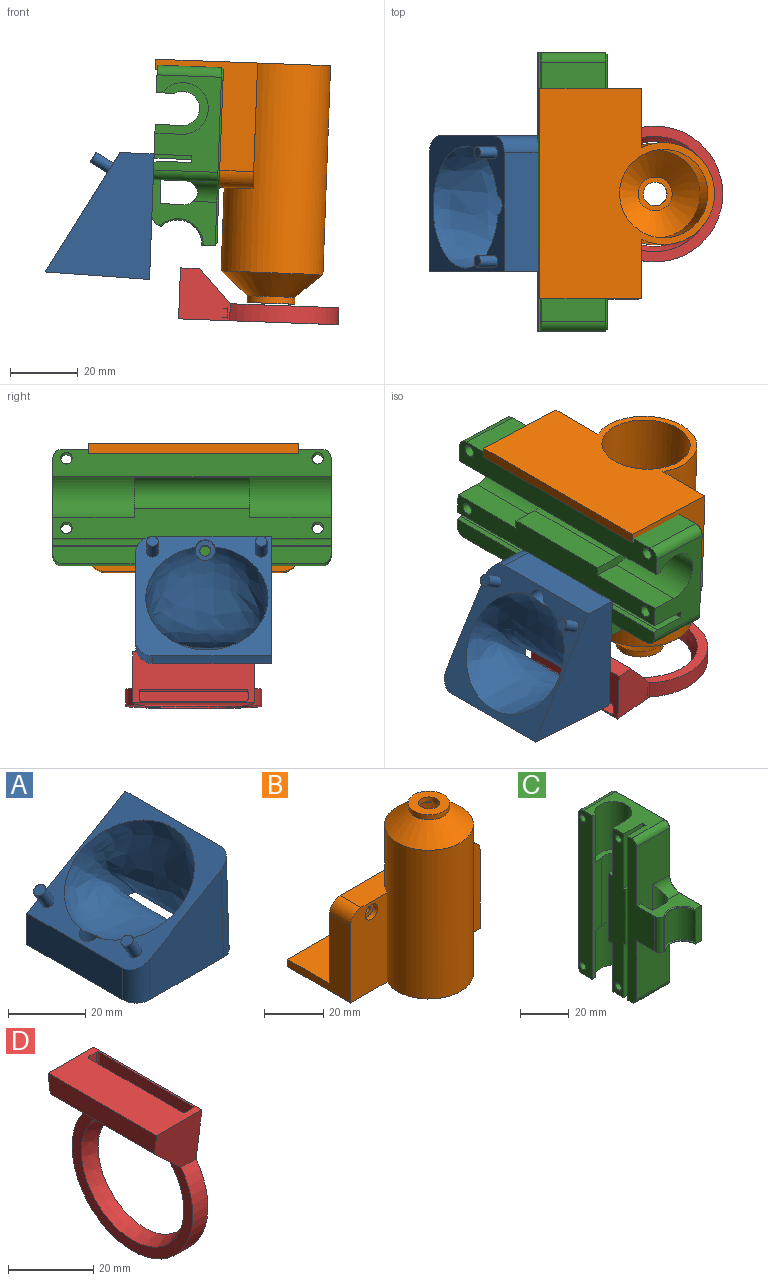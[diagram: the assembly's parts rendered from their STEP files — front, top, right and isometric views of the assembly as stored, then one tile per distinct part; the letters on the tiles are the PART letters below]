
ASSEMBLY  parts=4 mates=5
PART A: 17 faces, bbox 37.6x40.6x31.5 mm
  f0: plane 40.57x36.5mm, normal (-0.5,0,0.87), area 601.5mm2, adj f1,f3,f4,f5,f6,f8,f10,f11
  f1: plane 35x30.74mm, normal (1,0,0.03), area 1076.7mm2, adj f0,f2,f11,f16
  f2: plane 40.34x37.34mm, normal (0,0,-1), area 1343.6mm2, adj f1,f3,f4,f5,f10,f11,f15,f16
  f3: plane 35x10mm, normal (-1,0,0), area 350mm2, adj f0,f2,f10,f16
  f4: plane 27.91x27mm, normal (0,-1,0), area 544.5mm2, adj f0,f2,f10,f11
  f5: bspline ~35.97x33.55mm, area 2475.7mm2, adj f0,f2,f13
  f6: cylinder r=1.7mm len=6.9mm, axis (0.5,0,-0.87), area 64.1mm2, adj f0,f7
  f7: plane 3.4x2.94mm, normal (-0.5,0,0.87), area 9.1mm2, adj f6
  f8: cylinder r=1.7mm len=6.9mm, axis (0.5,0,-0.87), area 64.1mm2, adj f0,f9
  f9: plane 3.4x2.94mm, normal (-0.5,0,0.87), area 9.1mm2, adj f8
  f10: cylinder r=5mm len=12.89mm, axis (0,0,1), area 86.8mm2, adj f0,f2,f3,f4
  f11: cylinder r=5mm len=30.92mm, axis (0.03,0,-1), area 233.3mm2, adj f0,f1,f2,f4
  f12: cylinder r=1.6mm len=5.5mm, axis (0,0,-1), area 55.3mm2, adj f14,f15
  f13: cylinder r=3mm len=6mm, axis (0,0,-1), area 80.9mm2, adj f0,f5,f14
  f14: plane 6x6mm, normal (0,0,1), area 20.2mm2, adj f12,f13
  f15: cone r=1.6mm half-angle=45deg, axis (0,0,-1), area 8.2mm2, adj f2,f12
  f16: plane 37x30.74mm, normal (0,1,0), area 748.4mm2, adj f0,f1,f2,f3
PART B: 25 faces, bbox 62x51.5x70.6 mm
  f0: plane 62x51.5mm, normal (0,0,-1), area 1871.2mm2, adj f3,f4,f7,f13,f14,f15,f16
  f1: plane 62x20mm, normal (0,0,1), area 1240mm2, adj f2,f4,f14,f15
  f2: plane 62x34mm, normal (0,1,0), area 2085mm2, adj f1,f5,f6,f8,f14,f15,f17,f18
  f3: plane 37x17.48mm, normal (0,-1,0), area 613.2mm2, adj f0,f8,f10,f15,f16,f17
  f4: plane 62x3mm, normal (0,1,0), area 186mm2, adj f0,f1,f14,f15
  f5: cylinder r=1.4mm len=8mm, axis (0,-1,0), area 70.4mm2, adj f2,f11
  f6: cylinder r=1.4mm len=8mm, axis (0,-1,0), area 70.4mm2, adj f2,f9
  f7: plane 37x17.48mm, normal (0,-1,0), area 613.2mm2, adj f0,f8,f12,f14,f16,f18
  f8: plane 52x10mm, normal (0,0,1), area 355.3mm2, adj f2,f3,f7,f16,f17,f18
  f9: plane 6x6mm, normal (0,-1,0), area 22.1mm2, adj f6,f10
  f10: cylinder r=3mm len=6mm, axis (0,-1,0), area 37.7mm2, adj f3,f9
  f11: plane 6x6mm, normal (0,-1,0), area 22.1mm2, adj f5,f12
  f12: cylinder r=3mm len=6mm, axis (0,-1,0), area 37.7mm2, adj f7,f11
  f13: cylinder r=13mm len=61.55mm, axis (0,0,-1), area 5027.8mm2, adj f0,f19
  f14: plane 32x30mm, normal (-1,0,0), area 380mm2, adj f0,f1,f2,f4,f7,f18
  f15: plane 32x30mm, normal (1,0,0), area 380mm2, adj f0,f1,f2,f3,f4,f17
  f16: cylinder r=15mm len=61.55mm, axis (0,0,-1), area 4555.2mm2, adj f0,f3,f7,f8,f20
  f17: cylinder r=5mm len=10mm, axis (0,1,0), area 78.5mm2, adj f2,f3,f8,f15
  f18: cylinder r=5mm len=10mm, axis (0,-1,0), area 78.5mm2, adj f2,f7,f8,f14
  f19: cone r=13mm half-angle=48.8deg, axis (0,0,-1), area 601.1mm2, adj f13,f24
  f20: cone r=15mm half-angle=48.8deg, axis (0,0,-1), area 734.7mm2, adj f16,f21
  f21: cylinder r=7mm len=14mm, axis (0,0,1), area 88mm2, adj f20,f22
  f22: plane 14x14mm, normal (0,0,1), area 115.5mm2, adj f21,f23
  f23: cylinder r=3.5mm len=7mm, axis (0,0,1), area 44mm2, adj f22,f24
  f24: plane 10x10mm, normal (0,0,-1), area 40.1mm2, adj f19,f23
PART C: 75 faces, bbox 19.5x52.5x82.1 mm
  f0: cylinder r=7.55mm len=15.9mm, axis (0,0,-1), area 267.7mm2, adj f44,f47,f48,f50
  f1: plane 81x51.45mm, normal (1,0,0), area 2891.4mm2, adj f40,f41,f53,f54,f59,f60,f61,f62
  f2: plane 17.5x7mm, normal (0,1,0), area 122.5mm2, adj f4,f27,f29,f31
  f3: cylinder r=4mm len=29.5mm, axis (0,0,-1), area 134.5mm2, adj f4,f26,f28,f30
  f4: cylinder r=4mm len=18.59mm, axis (0,0,1), area 102.1mm2, adj f2,f3,f27,f28,f29,f30
  f5: plane 28x18.96mm, normal (0,0,1), area 309.8mm2, adj f7,f8,f12,f20,f22,f23,f33,f34
  f6: plane 28x18.96mm, normal (0,0,-1), area 309.8mm2, adj f9,f10,f12,f21,f22,f23,f32,f35
  f7: cylinder r=7.6mm len=24mm, axis (0,0,-1), area 748.1mm2, adj f5,f8,f12,f15
  f8: plane 24x7.86mm, normal (0,1,0), area 188.8mm2, adj f5,f7,f15,f36
  f9: cylinder r=7.6mm len=24mm, axis (0,0,-1), area 748.1mm2, adj f6,f10,f12,f16
  f10: plane 24x7.86mm, normal (0,1,0), area 188.8mm2, adj f6,f9,f16,f36
  f11: plane 76.3x18.96mm, normal (0,1,0), area 1447mm2, adj f32,f33,f38,f61
  f12: plane 82x5.42mm, normal (0,-1,0), area 262.8mm2, adj f5,f6,f7,f9,f13,f15,f16,f38
  f13: cylinder r=5mm len=34mm, axis (0,0,-1), area 621.1mm2, adj f12,f14,f15,f16
  f14: plane 34x7.86mm, normal (0,1,0), area 267.4mm2, adj f13,f15,f16,f36
  f15: plane 15.46x15.2mm, normal (0,0,1), area 85mm2, adj f7,f8,f12,f13,f14,f36
  f16: plane 15.46x15.2mm, normal (0,0,-1), area 85mm2, adj f9,f10,f12,f13,f14,f36
  f17: plane 10.96x1.15mm, normal (0,0,-1), area 12.6mm2, adj f18,f21,f23,f36
  f18: plane 27.33x10.96mm, normal (0,-1,0), area 299.7mm2, adj f17,f19,f23,f36
  f19: plane 10.96x1.15mm, normal (0,0,1), area 12.6mm2, adj f18,f20,f23,f36
  f20: plane 27.34x10.96mm, normal (0,-1,0), area 299.8mm2, adj f5,f19,f23,f36
  f21: plane 27.33x10.96mm, normal (0,-1,0), area 299.7mm2, adj f6,f17,f23,f36
  f22: plane 82x9.66mm, normal (0,1,0), area 792.5mm2, adj f5,f6,f23,f39
  f23: plane 82x2mm, normal (-1,0,0), area 132.6mm2, adj f5,f6,f17,f18,f19,f20,f21,f22
  f24: cylinder r=1.7mm len=18.96mm, axis (-1,0,0), area 202.6mm2, adj f38,f40
  f25: cylinder r=1.7mm len=18.96mm, axis (-1,0,0), area 202.6mm2, adj f38,f41
  f26: plane 76.3x18.96mm, normal (0,-1,0), area 1121.6mm2, adj f3,f27,f28,f29,f30,f31,f34,f35
  f27: plane 18.96x18.75mm, normal (0,0,-1), area 150mm2, adj f2,f4,f26,f28,f31,f37,f42,f43
  f28: cylinder r=6mm len=9.66mm, axis (1,0,0), area 65.7mm2, adj f3,f4,f26,f27,f71
  f29: plane 18.96x18.75mm, normal (0,0,1), area 150mm2, adj f2,f4,f26,f30,f31,f37,f45,f46
  f30: cylinder r=6mm len=9.66mm, axis (-1,0,0), area 65.7mm2, adj f3,f4,f26,f29,f70
  f31: plane 17.5x7mm, normal (1,0,0), area 122.5mm2, adj f2,f26,f27,f29
  f32: cylinder r=2.85mm len=18.96mm, axis (-1,0,0), area 84.9mm2, adj f6,f11,f38,f63
  f33: cylinder r=2.85mm len=18.96mm, axis (1,0,0), area 84.9mm2, adj f5,f11,f38,f62
  f34: cylinder r=2.85mm len=18.96mm, axis (-1,0,0), area 84.9mm2, adj f5,f26,f37,f66
  f35: cylinder r=2.85mm len=18.96mm, axis (1,0,0), area 84.9mm2, adj f6,f26,f37,f67
  f36: plane 82x9.95mm, normal (-1,0,0), area 610.1mm2, adj f5,f6,f8,f10,f14,f15,f16,f17
  f37: plane 82x15.43mm, normal (-1,0,0), area 587.5mm2, adj f5,f6,f26,f27,f29,f34,f35,f39
  f38: plane 82x8.09mm, normal (-1,0,0), area 641.8mm2, adj f5,f6,f11,f12,f24,f25,f32,f33
  f39: plane 82x1.3mm, normal (-0.34,0.94,0), area 113.4mm2, adj f5,f6,f22,f37
  f40: cone r=2.2mm half-angle=45deg, axis (1,0,0), area 8.7mm2, adj f1,f24,f61
  f41: cone r=1.7mm half-angle=45deg, axis (1,0,0), area 8.7mm2, adj f1,f25,f61
  f42: plane 0.8x0.44mm, normal (-0.71,-0.71,0), area 0.4mm2, adj f27,f43,f44,f48
  f43: torus R=7.55mm, axis (0,0,-1), area 10.8mm2, adj f27,f42,f44,f50
  f44: torus R=7.55mm, axis (0,0,-1), area 10.9mm2, adj f0,f42,f43,f48,f50
  f45: plane 0.8x0.44mm, normal (-0.71,-0.71,0), area 0.4mm2, adj f29,f46,f47,f48
  f46: torus R=7.55mm, axis (0,0,-1), area 10.8mm2, adj f29,f45,f47,f50
  f47: torus R=7.55mm, axis (0,0,1), area 10.9mm2, adj f0,f45,f46,f48,f50
  f48: cylinder r=3mm len=17.5mm, axis (0,0,-1), area 20.2mm2, adj f0,f27,f29,f42,f44,f45,f47,f49
  f49: cylinder r=3mm len=17.5mm, axis (0,0,-1), area 67.1mm2, adj f27,f29,f37,f48
  f50: plane 17.5x3.95mm, normal (0,-1,0), area 62.6mm2, adj f0,f27,f29,f43,f44,f46,f47,f74
  f51: cylinder r=1.7mm len=18.96mm, axis (-1,0,0), area 202.6mm2, adj f36,f53
  f52: cylinder r=1.7mm len=18.96mm, axis (-1,0,0), area 202.6mm2, adj f36,f54
  f53: cone r=2.2mm half-angle=45deg, axis (1,0,0), area 8.7mm2, adj f1,f51
  f54: cone r=2.2mm half-angle=45deg, axis (1,0,0), area 8.7mm2, adj f1,f52
  f55: cylinder r=1.25mm len=8.96mm, axis (-1,0,0), area 70.4mm2, adj f56,f59
  f56: plane 2.5x2.5mm, normal (1,0,0), area 4.9mm2, adj f55
  f57: cylinder r=1.25mm len=8.96mm, axis (-1,0,0), area 70.4mm2, adj f58,f60
  f58: plane 2.5x2.5mm, normal (1,0,0), area 4.9mm2, adj f57
  f59: cone r=1.25mm half-angle=45deg, axis (1,0,0), area 6.7mm2, adj f1,f55
  f60: cone r=1.25mm half-angle=45deg, axis (1,0,0), area 6.7mm2, adj f1,f57
  f61: plane 76.36x0.56mm, normal (0.71,0.71,0), area 53.9mm2, adj f1,f11,f40,f41,f62,f63
  f62: cone r=2.35mm half-angle=45deg, axis (-1,0,0), area 2.9mm2, adj f1,f33,f61,f64
  f63: cone r=2.35mm half-angle=45deg, axis (-1,0,0), area 2.9mm2, adj f1,f32,f61,f65
  f64: plane 28x0.5mm, normal (0.71,0,0.71), area 19.8mm2, adj f1,f5,f62,f66
  f65: plane 28x0.5mm, normal (0.71,0,-0.71), area 19.8mm2, adj f1,f6,f63,f67
  f66: cone r=2.35mm half-angle=45deg, axis (-1,0,0), area 2.9mm2, adj f1,f34,f64,f68
  f67: cone r=2.35mm half-angle=45deg, axis (-1,0,0), area 2.9mm2, adj f1,f35,f65,f69
  f68: plane 23.4x0.5mm, normal (0.71,-0.71,0), area 16.5mm2, adj f1,f26,f66,f70
  f69: plane 23.4x0.5mm, normal (0.71,-0.71,0), area 16.5mm2, adj f1,f26,f67,f71
  f70: cone r=6.5mm half-angle=45deg, axis (1,0,0), area 6.9mm2, adj f1,f30,f68,f72
  f71: cone r=6.5mm half-angle=45deg, axis (1,0,0), area 6.9mm2, adj f1,f28,f69,f73
  f72: plane 12.75x0.5mm, normal (0.71,0,0.71), area 8.8mm2, adj f1,f29,f70,f74
  f73: plane 12.75x0.5mm, normal (0.71,0,-0.71), area 8.8mm2, adj f1,f27,f71,f74
  f74: plane 17.5x0.5mm, normal (0.71,-0.71,0), area 12mm2, adj f1,f50,f72,f73
PART D: 24 faces, bbox 15.1x42.7x48.4 mm
  f0: plane 40x31.94mm, normal (-1,0,0), area 254.2mm2, adj f1,f7,f11
  f1: cone r=16.98mm half-angle=21deg, axis (-1,0,0), area 333.6mm2, adj f0,f2,f11
  f2: plane 31.68x27.78mm, normal (1,0,0), area 30.5mm2, adj f1,f3,f11
  f3: cone r=15.84mm half-angle=21deg, axis (-1,0,0), area 200.2mm2, adj f2,f4,f11
  f4: torus R=18.16mm, axis (-1,0,0), area 475.6mm2, adj f3,f5,f11
  f5: cone r=17.2mm half-angle=56deg, axis (-1,0,0), area 180.3mm2, adj f4,f6,f11
  f6: cylinder r=17.2mm len=34.4mm, axis (-1,0,0), area 32.2mm2, adj f5,f8,f11
  f7: cylinder r=20mm len=40mm, axis (-1,0,0), area 442.1mm2, adj f0,f8,f10,f12
  f8: plane 46.98x40mm, normal (1,0,0), area 748.2mm2, adj f6,f7,f9,f10,f11,f12
  f9: plane 36x15mm, normal (0,0,1), area 428.2mm2, adj f8,f10,f12,f13,f15,f16,f17,f18
  f10: plane 15.04x15mm, normal (0,-0.99,-0.13), area 179.8mm2, adj f7,f8,f9,f11,f13,f14
  f11: plane 32.21x5.13mm, normal (0,0,-1), area 137.7mm2, adj f0,f1,f2,f3,f4,f5,f6,f8
  f12: plane 15.04x15mm, normal (0,0.99,-0.13), area 179.8mm2, adj f7,f8,f9,f11,f13,f14
  f13: plane 36x5.58mm, normal (-1,0,0), area 196.9mm2, adj f9,f10,f12,f14
  f14: plane 34.55x9.99mm, normal (-0.69,0,-0.73), area 458.4mm2, adj f10,f11,f12,f13
  f15: plane 31x14.33mm, normal (1,0,0), area 444.3mm2, adj f9,f16,f22,f23
  f16: extruded ~14.33x0.5mm, area 11.2mm2, adj f9,f15,f17,f23
  f17: plane 14.33x2.5mm, normal (0,-1,0), area 35.8mm2, adj f9,f16,f18,f23
  f18: extruded ~14.33x0.5mm, area 11.2mm2, adj f9,f17,f19,f23
  f19: plane 31x14.33mm, normal (-1,0,0), area 444.3mm2, adj f9,f18,f20,f23
  f20: extruded ~14.33x0.5mm, area 11.2mm2, adj f9,f19,f21,f23
  f21: plane 14.33x2.5mm, normal (0,1,0), area 35.8mm2, adj f9,f20,f22,f23
  f22: extruded ~14.33x0.5mm, area 11.2mm2, adj f9,f15,f21,f23
  f23: plane 32x3.5mm, normal (0,0,1), area 111.8mm2, adj f15,f16,f17,f18,f19,f20,f21,f22
PLACE A rot(axis=(-0.69,0,0.72),180deg) t=(-86.69,-53.18,-22.93)mm
PLACE B rot(axis=(0.71,-0.71,-0.01),178.5deg) t=(-30.16,-30.29,-72.75)mm
PLACE C rot(axis=(1,0.02,-0.02),90deg) t=(-55.77,11.21,-4.39)mm
PLACE D rot(axis=(-0.69,0,0.72),180deg) t=(-78.79,-49.29,-34.5)mm
MATE cylindrical B.f5 <-> C.f55  axis (-1,0,0.04) through (-44.85,-9.29,-23.33)mm
MATE slider D.f6 <-> B.f13  axis (0.04,0,1) through (-29.78,-30.29,-62.32)mm
MATE planar C.f1 <-> B.f2  axis (1,0,-0.04) through (-44.44,-29.79,-12.06)mm
MATE planar A.f2 <-> C.f37  axis (1,0,-0.04) through (-64.76,-33.24,-35.04)mm
MATE planar C.f11 <-> B.f1  axis (0.04,0,1) through (-53.69,-29.79,7.99)mm
